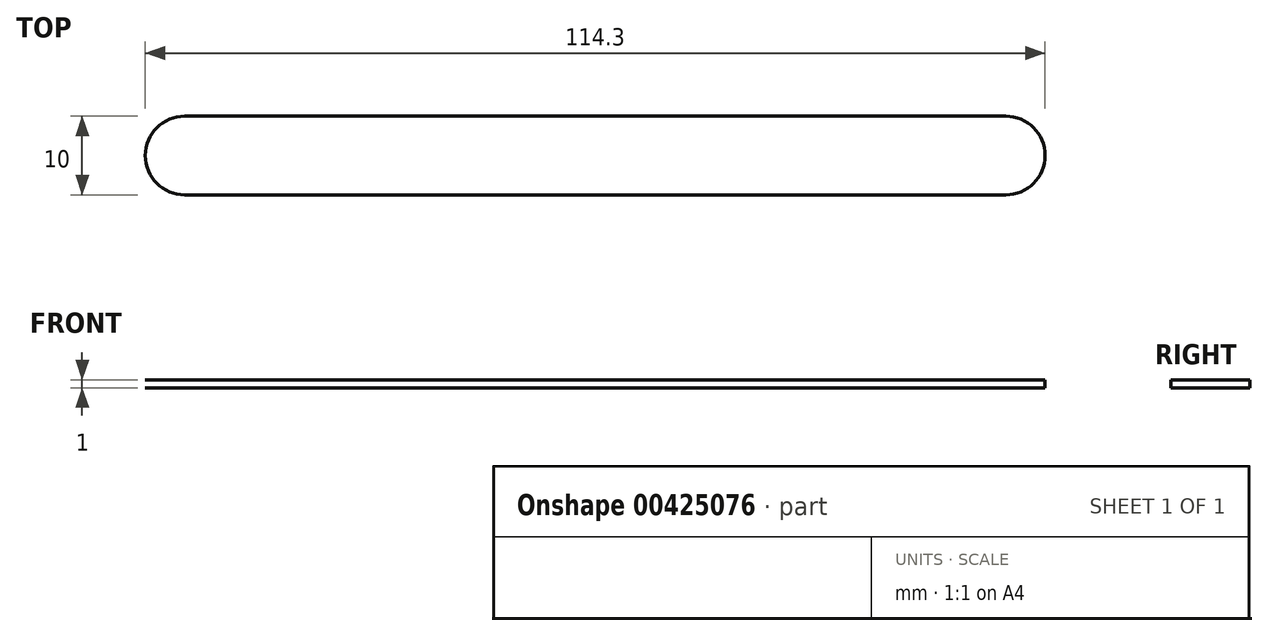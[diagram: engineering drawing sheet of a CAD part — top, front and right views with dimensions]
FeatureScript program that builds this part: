
annotation { "Feature Type Name" : "Feature", "Feature Type Description" : "" }
export const myFeature = defineFeature(function(context is Context, id is Id, definition is map)
    precondition{}
    {
        {
            var Q0;
            Q0=qCreatedBy(makeId("Top.planeOp"),FACE);
            var sketch = newSketch(context, id + "F0", { "sketchPlane" : qUnion([Q0])});
            skLineSegment(sketch, "E0.bottom", {"start": v(-44.13, 10) * mm, "end": v(60.16, 10) * mm});
            skLineSegment(sketch, "E0.top", {"start": v(-44.13, 0) * mm, "end": v(60.16, 0) * mm});
            skLineSegment(sketch, "E0.left", {"start": v(-49.13, 5) * mm, "end": v(-49.13, 5) * mm});
            skLineSegment(sketch, "E0.right", {"start": v(65.17, 5) * mm, "end": v(65.17, 5) * mm});
            skPoint(sketch, "E1.visualSharp", {"position": v(-49.13, 10) * mm});
            skArc(sketch, "E1.filletArc", {"start": v(-44.13, 10) * mm, "mid": v(-47.67, 8.53) * mm, "end": v(-49.13, 5) * mm});
            skPoint(sketch, "E2.visualSharp", {"position": v(-49.13, 0) * mm});
            skArc(sketch, "E2.filletArc", {"start": v(-49.13, 5) * mm, "mid": v(-47.67, 1.47) * mm, "end": v(-44.13, 0) * mm});
            skPoint(sketch, "E3.visualSharp", {"position": v(65.17, 10) * mm});
            skArc(sketch, "E3.filletArc", {"start": v(65.17, 5) * mm, "mid": v(63.7, 8.53) * mm, "end": v(60.16, 10) * mm});
            skPoint(sketch, "E4.visualSharp", {"position": v(65.17, 0) * mm});
            skArc(sketch, "E4.filletArc", {"start": v(60.16, 0) * mm, "mid": v(63.7, 1.47) * mm, "end": v(65.17, 5) * mm});
            skSolve(sketch);
        }
        {
            var Q0;
            Q0=makeQuery(id+"F0.imprint","IMPRINT",FACE,{"disambiguationData":[TD([[makeQuery(id+"F0.imprint","IMPRINT",EDGE,{"derivedFrom":sQuery(id+"F0.wireOp",EDGE,"E0.bottom")}),-1.0]])]});
            extrude(context, id + "F1", {"entities" : qUnion([Q0]), "depth" : 1 * mm});
        }
    });
